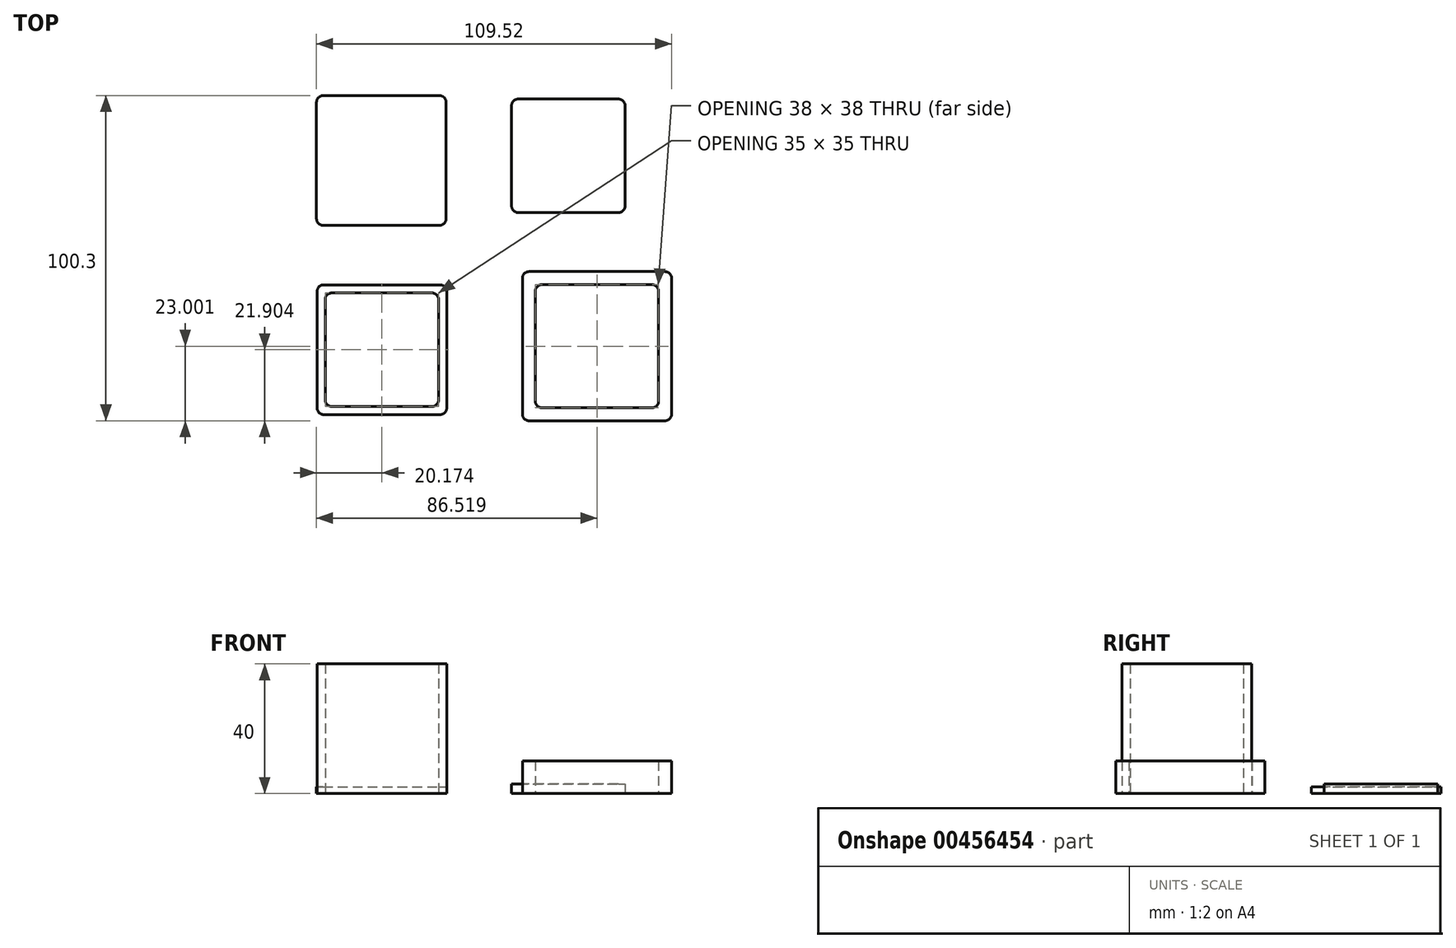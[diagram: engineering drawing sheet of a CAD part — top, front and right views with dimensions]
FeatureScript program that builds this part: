
annotation { "Feature Type Name" : "Feature", "Feature Type Description" : "" }
export const myFeature = defineFeature(function(context is Context, id is Id, definition is map)
    precondition{}
    {
        {
            var Q0;
            Q0=qCreatedBy(makeId("Top.planeOp"),FACE);
            var sketch = newSketch(context, id + "F0", { "sketchPlane" : qUnion([Q0])});
            skLineSegment(sketch, "E0", {"start": v(-49.46, 42.86) * mm, "end": v(-9.46, 42.86) * mm});
            skLineSegment(sketch, "E1", {"start": v(-9.46, 42.86) * mm, "end": v(-9.46, 2.86) * mm});
            skLineSegment(sketch, "E2", {"start": v(-9.46, 2.86) * mm, "end": v(-49.46, 2.86) * mm});
            skLineSegment(sketch, "E3", {"start": v(-49.46, 2.86) * mm, "end": v(-49.46, 42.86) * mm});
            skSolve(sketch);
        }
        {
            var Q0;
            Q0=makeQuery(id+"F0.imprint","IMPRINT",FACE,{"disambiguationData":[TD([[makeQuery(id+"F0.imprint","IMPRINT",EDGE,{"derivedFrom":sQuery(id+"F0.wireOp",EDGE,"E0")}),-1.0]])]});
            extrude(context, id + "F1", {"entities" : qUnion([Q0]), "depth" : 2 * mm});
        }
        {
            var Q0;
            Q0=makeQuery(id+"F1.opExtrude","SWEPT_EDGE",EDGE,{"disambiguationData":[OSD([sQuery(id+"F0.wireOp",EDGE,"E2"),sQuery(id+"F0.wireOp",EDGE,"E3")])]});
            var Q1;
            Q1=makeQuery(id+"F1.opExtrude","SWEPT_EDGE",EDGE,{"disambiguationData":[OSD([sQuery(id+"F0.wireOp",EDGE,"E1"),sQuery(id+"F0.wireOp",EDGE,"E2")])]});
            var Q2;
            Q2=makeQuery(id+"F1.opExtrude","SWEPT_EDGE",EDGE,{"disambiguationData":[OSD([sQuery(id+"F0.wireOp",EDGE,"E0"),sQuery(id+"F0.wireOp",EDGE,"E1")])]});
            var Q3;
            Q3=makeQuery(id+"F1.opExtrude","SWEPT_EDGE",EDGE,{"disambiguationData":[OSD([sQuery(id+"F0.wireOp",EDGE,"E0"),sQuery(id+"F0.wireOp",EDGE,"E3")])]});
            fillet(context, id + "F2", {"entities" : qUnion([Q0, Q1, Q2, Q3]), "radius" : 2 * mm, "tangentPropagation" : true, "allowEdgeOverflow" : false});
        }
        {
            var Q0;
            Q0=qCreatedBy(makeId("Top.planeOp"),FACE);
            var sketch = newSketch(context, id + "F3", { "sketchPlane" : qUnion([Q0])});
            skLineSegment(sketch, "E4", {"start": v(10.71, 41.79) * mm, "end": v(45.71, 41.79) * mm});
            skLineSegment(sketch, "E5", {"start": v(45.71, 41.79) * mm, "end": v(45.71, 6.79) * mm});
            skLineSegment(sketch, "E6", {"start": v(45.71, 6.79) * mm, "end": v(10.71, 6.79) * mm});
            skLineSegment(sketch, "E7", {"start": v(10.71, 6.79) * mm, "end": v(10.71, 41.79) * mm});
            skSolve(sketch);
        }
        {
            var Q0;
            Q0=makeQuery(id+"F3.imprint","IMPRINT",FACE,{"disambiguationData":[TD([[makeQuery(id+"F3.imprint","IMPRINT",EDGE,{"derivedFrom":sQuery(id+"F3.wireOp",EDGE,"E4")}),-1.0]])]});
            extrude(context, id + "F4", {"entities" : qUnion([Q0]), "depth" : 3 * mm});
        }
        {
            var Q0;
            Q0=makeQuery(id+"F4.opExtrude","SWEPT_EDGE",EDGE,{"disambiguationData":[OSD([sQuery(id+"F3.wireOp",EDGE,"E6"),sQuery(id+"F3.wireOp",EDGE,"E7")])]});
            var Q1;
            Q1=makeQuery(id+"F4.opExtrude","SWEPT_EDGE",EDGE,{"disambiguationData":[OSD([sQuery(id+"F3.wireOp",EDGE,"E5"),sQuery(id+"F3.wireOp",EDGE,"E6")])]});
            var Q2;
            Q2=makeQuery(id+"F4.opExtrude","SWEPT_EDGE",EDGE,{"disambiguationData":[OSD([sQuery(id+"F3.wireOp",EDGE,"E4"),sQuery(id+"F3.wireOp",EDGE,"E5")])]});
            var Q3;
            Q3=makeQuery(id+"F4.opExtrude","SWEPT_EDGE",EDGE,{"disambiguationData":[OSD([sQuery(id+"F3.wireOp",EDGE,"E4"),sQuery(id+"F3.wireOp",EDGE,"E7")])]});
            fillet(context, id + "F5", {"entities" : qUnion([Q0, Q1, Q2, Q3]), "radius" : 2 * mm, "tangentPropagation" : true, "allowEdgeOverflow" : false});
        }
        {
            var Q0;
            Q0=qCreatedBy(makeId("Top.planeOp"),FACE);
            var sketch = newSketch(context, id + "F6", { "sketchPlane" : qUnion([Q0])});
            skLineSegment(sketch, "E8", {"start": v(-49.29, -15.54) * mm, "end": v(-49.29, -55.54) * mm});
            skLineSegment(sketch, "E9", {"start": v(-49.29, -55.54) * mm, "end": v(-9.29, -55.54) * mm});
            skLineSegment(sketch, "E10", {"start": v(-9.29, -55.54) * mm, "end": v(-9.29, -15.54) * mm});
            skLineSegment(sketch, "E11", {"start": v(-9.29, -15.54) * mm, "end": v(-49.29, -15.54) * mm});
            skSolve(sketch);
        }
        {
            var Q0;
            Q0=makeQuery(id+"F6.imprint","IMPRINT",FACE,{"disambiguationData":[TD([[makeQuery(id+"F6.imprint","IMPRINT",EDGE,{"derivedFrom":sQuery(id+"F6.wireOp",EDGE,"E8")}),1.0]])]});
            extrude(context, id + "F7", {"entities" : qUnion([Q0]), "depth" : 40 * mm});
        }
        {
            var Q0;
            Q0=makeQuery(id+"F7.opExtrude","CAP_FACE",FACE,{"disambiguationData":[OSD([sQuery(id+"F6.wireOp",EDGE,"E8"),sQuery(id+"F6.wireOp",EDGE,"E9"),sQuery(id+"F6.wireOp",EDGE,"E10"),sQuery(id+"F6.wireOp",EDGE,"E11")])],"isStart":false});
            var Q1;
            Q1=makeQuery(id+"F7.opExtrude","CAP_FACE",FACE,{"disambiguationData":[OSD([sQuery(id+"F6.wireOp",EDGE,"E8"),sQuery(id+"F6.wireOp",EDGE,"E9"),sQuery(id+"F6.wireOp",EDGE,"E10"),sQuery(id+"F6.wireOp",EDGE,"E11")])],"isStart":true});
            shell(context, id + "F8", {"entities" : qUnion([Q0, Q1]), "thickness" : 2.5 * mm});
        }
        {
            var Q0;
            Q0=makeQuery(id+"F7.opExtrude","SWEPT_EDGE",EDGE,{"disambiguationData":[OSD([sQuery(id+"F6.wireOp",EDGE,"E9"),sQuery(id+"F6.wireOp",EDGE,"E10")])]});
            var Q1;
            Q1=makeQuery(id+"F7.opExtrude","SWEPT_EDGE",EDGE,{"disambiguationData":[OSD([sQuery(id+"F6.wireOp",EDGE,"E10"),sQuery(id+"F6.wireOp",EDGE,"E11")])]});
            var Q2;
            Q2=makeQuery(id+"F7.opExtrude","SWEPT_EDGE",EDGE,{"disambiguationData":[OSD([sQuery(id+"F6.wireOp",EDGE,"E8"),sQuery(id+"F6.wireOp",EDGE,"E11")])]});
            var Q3;
            Q3=makeQuery(id+"F7.opExtrude","SWEPT_EDGE",EDGE,{"disambiguationData":[OSD([sQuery(id+"F6.wireOp",EDGE,"E8"),sQuery(id+"F6.wireOp",EDGE,"E9")])]});
            var Q4;
            Q4=makeQuery(id+"F8.opShell","OFFSET_EDGE",EDGE,{"disambiguationData":[OSD([sQuery(id+"F6.wireOp",EDGE,"E9"),sQuery(id+"F6.wireOp",EDGE,"E10")])]});
            var Q5;
            Q5=makeQuery(id+"F8.opShell","OFFSET_EDGE",EDGE,{"disambiguationData":[OSD([sQuery(id+"F6.wireOp",EDGE,"E10"),sQuery(id+"F6.wireOp",EDGE,"E11")])]});
            var Q6;
            Q6=makeQuery(id+"F8.opShell","OFFSET_EDGE",EDGE,{"disambiguationData":[OSD([sQuery(id+"F6.wireOp",EDGE,"E8"),sQuery(id+"F6.wireOp",EDGE,"E11")])]});
            var Q7;
            Q7=makeQuery(id+"F8.opShell","OFFSET_EDGE",EDGE,{"disambiguationData":[OSD([sQuery(id+"F6.wireOp",EDGE,"E8"),sQuery(id+"F6.wireOp",EDGE,"E9")])]});
            fillet(context, id + "F9", {"entities" : qUnion([Q0, Q1, Q2, Q3, Q4, Q5, Q6, Q7]), "radius" : 2 * mm, "tangentPropagation" : true, "allowEdgeOverflow" : false});
        }
        {
            var Q0;
            Q0=qCreatedBy(makeId("Top.planeOp"),FACE);
            var sketch = newSketch(context, id + "F10", { "sketchPlane" : qUnion([Q0])});
            skLineSegment(sketch, "E12", {"start": v(14.06, -11.44) * mm, "end": v(60.06, -11.44) * mm});
            skLineSegment(sketch, "E13", {"start": v(60.06, -11.44) * mm, "end": v(60.06, -57.44) * mm});
            skLineSegment(sketch, "E14", {"start": v(60.06, -57.44) * mm, "end": v(14.06, -57.44) * mm});
            skLineSegment(sketch, "E15", {"start": v(14.06, -57.44) * mm, "end": v(14.06, -11.44) * mm});
            skSolve(sketch);
        }
        {
            var Q0;
            Q0=makeQuery(id+"F10.imprint","IMPRINT",FACE,{"disambiguationData":[TD([[makeQuery(id+"F10.imprint","IMPRINT",EDGE,{"derivedFrom":sQuery(id+"F10.wireOp",EDGE,"E12")}),-1.0]])]});
            extrude(context, id + "F11", {"entities" : qUnion([Q0]), "depth" : 10 * mm});
        }
        {
            var Q0;
            Q0=makeQuery(id+"F11.opExtrude","CAP_FACE",FACE,{"disambiguationData":[OSD([sQuery(id+"F10.wireOp",EDGE,"E12"),sQuery(id+"F10.wireOp",EDGE,"E13"),sQuery(id+"F10.wireOp",EDGE,"E14"),sQuery(id+"F10.wireOp",EDGE,"E15")])],"isStart":false});
            var Q1;
            Q1=makeQuery(id+"F11.opExtrude","CAP_FACE",FACE,{"disambiguationData":[OSD([sQuery(id+"F10.wireOp",EDGE,"E12"),sQuery(id+"F10.wireOp",EDGE,"E13"),sQuery(id+"F10.wireOp",EDGE,"E14"),sQuery(id+"F10.wireOp",EDGE,"E15")])],"isStart":true});
            shell(context, id + "F12", {"entities" : qUnion([Q0, Q1]), "thickness" : 4 * mm});
        }
        {
            var Q0;
            Q0=makeQuery(id+"F11.opExtrude","SWEPT_EDGE",EDGE,{"disambiguationData":[OSD([sQuery(id+"F10.wireOp",EDGE,"E12"),sQuery(id+"F10.wireOp",EDGE,"E13")])]});
            var Q1;
            Q1=makeQuery(id+"F11.opExtrude","SWEPT_EDGE",EDGE,{"disambiguationData":[OSD([sQuery(id+"F10.wireOp",EDGE,"E14"),sQuery(id+"F10.wireOp",EDGE,"E15")])]});
            var Q2;
            Q2=makeQuery(id+"F11.opExtrude","SWEPT_EDGE",EDGE,{"disambiguationData":[OSD([sQuery(id+"F10.wireOp",EDGE,"E12"),sQuery(id+"F10.wireOp",EDGE,"E15")])]});
            var Q3;
            Q3=makeQuery(id+"F11.opExtrude","SWEPT_EDGE",EDGE,{"disambiguationData":[OSD([sQuery(id+"F10.wireOp",EDGE,"E13"),sQuery(id+"F10.wireOp",EDGE,"E14")])]});
            var Q4;
            Q4=makeQuery(id+"F12.opShell","OFFSET_EDGE",EDGE,{"disambiguationData":[OSD([sQuery(id+"F10.wireOp",EDGE,"E14"),sQuery(id+"F10.wireOp",EDGE,"E15")])]});
            var Q5;
            Q5=makeQuery(id+"F12.opShell","OFFSET_EDGE",EDGE,{"disambiguationData":[OSD([sQuery(id+"F10.wireOp",EDGE,"E12"),sQuery(id+"F10.wireOp",EDGE,"E15")])]});
            var Q6;
            Q6=makeQuery(id+"F12.opShell","OFFSET_EDGE",EDGE,{"disambiguationData":[OSD([sQuery(id+"F10.wireOp",EDGE,"E13"),sQuery(id+"F10.wireOp",EDGE,"E14")])]});
            var Q7;
            Q7=makeQuery(id+"F12.opShell","OFFSET_EDGE",EDGE,{"disambiguationData":[OSD([sQuery(id+"F10.wireOp",EDGE,"E12"),sQuery(id+"F10.wireOp",EDGE,"E13")])]});
            fillet(context, id + "F13", {"entities" : qUnion([Q0, Q1, Q2, Q3, Q4, Q5, Q6, Q7]), "radius" : 2 * mm, "tangentPropagation" : true, "allowEdgeOverflow" : false});
        }
    });
